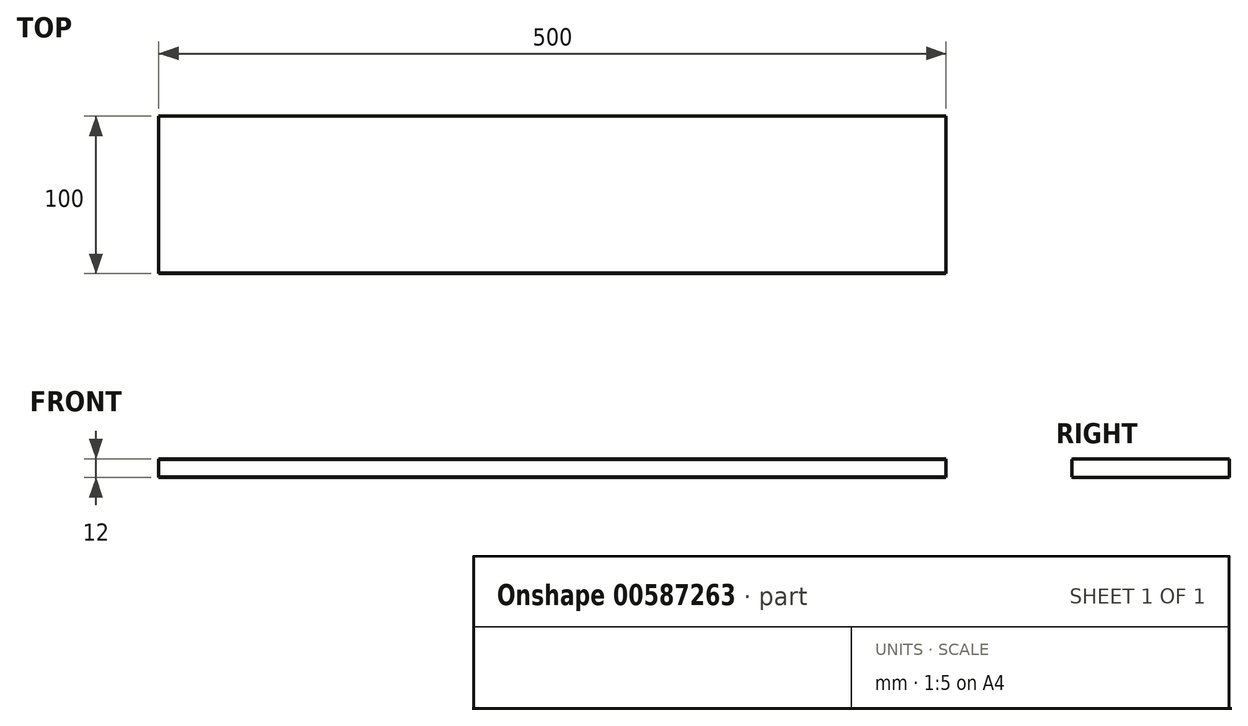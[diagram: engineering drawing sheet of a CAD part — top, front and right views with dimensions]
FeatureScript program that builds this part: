
annotation { "Feature Type Name" : "Feature", "Feature Type Description" : "" }
export const myFeature = defineFeature(function(context is Context, id is Id, definition is map)
    precondition{}
    {
        {
            var Q0;
            Q0=qCreatedBy(makeId("Right.planeOp"),FACE);
            var sketch = newSketch(context, id + "F0", { "sketchPlane" : qUnion([Q0])});
            skLineSegment(sketch, "E0.bottom", {"start": v(0, 6) * mm, "end": v(100, 6) * mm});
            skLineSegment(sketch, "E0.top", {"start": v(0, -6) * mm, "end": v(100, -6) * mm});
            skLineSegment(sketch, "E0.left", {"start": v(0, 6) * mm, "end": v(0, -6) * mm});
            skLineSegment(sketch, "E0.right", {"start": v(100, 6) * mm, "end": v(100, -6) * mm});
            skSolve(sketch);
        }
        {
            var Q0;
            Q0=makeQuery(id+"F0.imprint","IMPRINT",FACE,{"disambiguationData":[TD([[makeQuery(id+"F0.imprint","IMPRINT",EDGE,{"derivedFrom":sQuery(id+"F0.wireOp",EDGE,"E0.bottom")}),-1.0]])]});
            extrude(context, id + "F1", {"entities" : qUnion([Q0]), "endBound" : BoundingType.SYMMETRIC, "depth" : 500 * mm, "offsetDistance" : 25 * mm});
        }
        {
            var Q0;
            Q0=makeQuery(id+"F1.opExtrude","SWEPT_EDGE",EDGE,{"disambiguationData":[OSD([sQuery(id+"F0.wireOp",EDGE,"E0.bottom"),sQuery(id+"F0.wireOp",EDGE,"E0.left")])]});
            var Q1;
            Q1=makeQuery(id+"F1.opExtrude","SWEPT_EDGE",EDGE,{"disambiguationData":[OSD([sQuery(id+"F0.wireOp",EDGE,"E0.top"),sQuery(id+"F0.wireOp",EDGE,"E0.left")])]});
            chamfer(context, id + "F2", {"entities" : qUnion([Q0, Q1]), "width" : 0.5 * mm, "tangentPropagation" : true});
        }
    });
